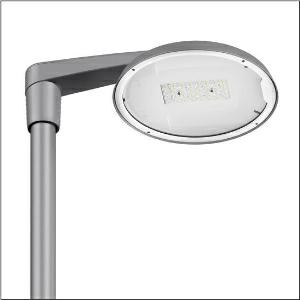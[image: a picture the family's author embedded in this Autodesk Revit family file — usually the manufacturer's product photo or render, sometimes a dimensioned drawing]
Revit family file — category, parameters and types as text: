
# Revit family: dl_50_iq_mini___st0_5a_5xa248b31f08je_6363
name_source: partatom
category: Lighting Fixtures
units: mm (PartAtom-declared; Revit-internal decimal feet)

## family parameters
Cut with Voids When Loaded = No
Host = Face
Light Source = No
Part Type = Normal
Room Calculation Point = No
Round Connector Dimension = Use Diameter
Shared = No

## types (1)
- --- (1 x LED, 10300 lm, 66 W, 3000K)
    Apparent Load = 66 VA
    CIE Flux Codes = 43 76 97 100 100
    Color Rendering = 70
    Color Temperature = 3000K
    Default Elevation = 1800 mm
    Description = DL 50 iQ mini, mast luminaire, primary light control with lens, of PMMA, primary optical cover: cover, of toughened safety glass, transparent, light distribution: ST0.5a, light emission: direct distribution, primary light characteristic: asymmetric, installation type: side-entry, post-top, LED, High Power LED, rated luminous flux: 10.300lm, luminous efficacy: 156lm/W, light colour: 730, colour temperature: 3000K, control gear: iQ Street-Remote, control: optimised constant luminous flux control (CLO 2.0), Desk-Remote (wireless, voltage-free reading and setting of iQ features in the workshop via application-optimized NFC function/RFID function), Light-Fading, Smart-Wire, Night-Set, Lumen-Switch, Temp-Guard, Auto-Match, Street-Remote, mains connection: 230..240V, AC, 50/60Hz, connection cable pre-assembled, cable length: 8,5m, start of lifetime: 66W, end of service life: 69W, reduction: 30W, luminaire housing, of diecast aluminium, powder-coated, SITECO metallic grey (DB 702S), inclination adjustable: 0°, 5°, 10° (post-top) | 0°, -5°, -10°, -15° (side-entry), please order mast post-top element or mast side-entry element separately, diameter: 500mm, height: 115mm, post-top: for spigot size d x l = 76 x 100mm; with reducer (optional accessory) 60 x 100mm | side-entry: for spigot size d x l = 60 x 100mm; with reducer (optional accessory) 42 x 100mm, mounting height: 4..6m, protection rating (complete): IP66, insulation class (complete): insulation class II (safety insulation), certification: CE, ENEC, ENEC+, VDE, impact resistance: IK08, permissible operating ambient temperature for outdoor applications: -25..+40°C, standard-compliant lighting for roads and squares, packaging unit: 1 piece

Light Distribution: ST0.5a
    Height = 115 mm
    Lamp = 1 x LED
    Lamp Light Flux = 10300 lm
    Lamp Power = 66 W
    Lamp count = 1
    Length = 500 mm
    Luminous efficacy = 156 lm/W
    Manufacturer = Siteco
    ModVariant = No
    Model = 5XA248B31F08JE
    Mounting Place = Pole
    Mounting Type = Pole top
    Number of Poles = 1
    OnlyDefault = Yes
    Power Factor = 1
    Product Name = DL 50 iQ mini | ST0.5a
    Product group = mast luminaire | pylon top
    ProductGroupID = 6100
    Protection Class = Protection class II
    Protection Degree = IP 66
    RLX_Detail_Level = 1
    RLX_Emergency_Light_Flux = 0 lm
    RLX_Emergency_Type = 0
    RLX_Emergency_Type_DB = No
    RlxData = <blob elided: 126905 chars, md5=49e58f79>
    Socket = socket
    Standby Power = 0 W
    System Light Flux = 10300 lm
    System Power = 66 W
    Type Comments = factory setting: luminous flux: 100 % | dim-lin: 254 | 693 mA
    Type Image = l_1251794.jpg
    URL = http://relux.com
    VarID = @adj_143971
    Voltage = 0 V
    Weight = 0.00 kg
    Width = 0 mm  [stored 0 ft]

note: [stored X ft] marks values corroborated as IEEE doubles in the binary element streams (Revit-internal decimal feet)

## geometry (parser evidence)
native form markers: Blend x4, Sweep x12
no freeform markers — native parametric forms only
